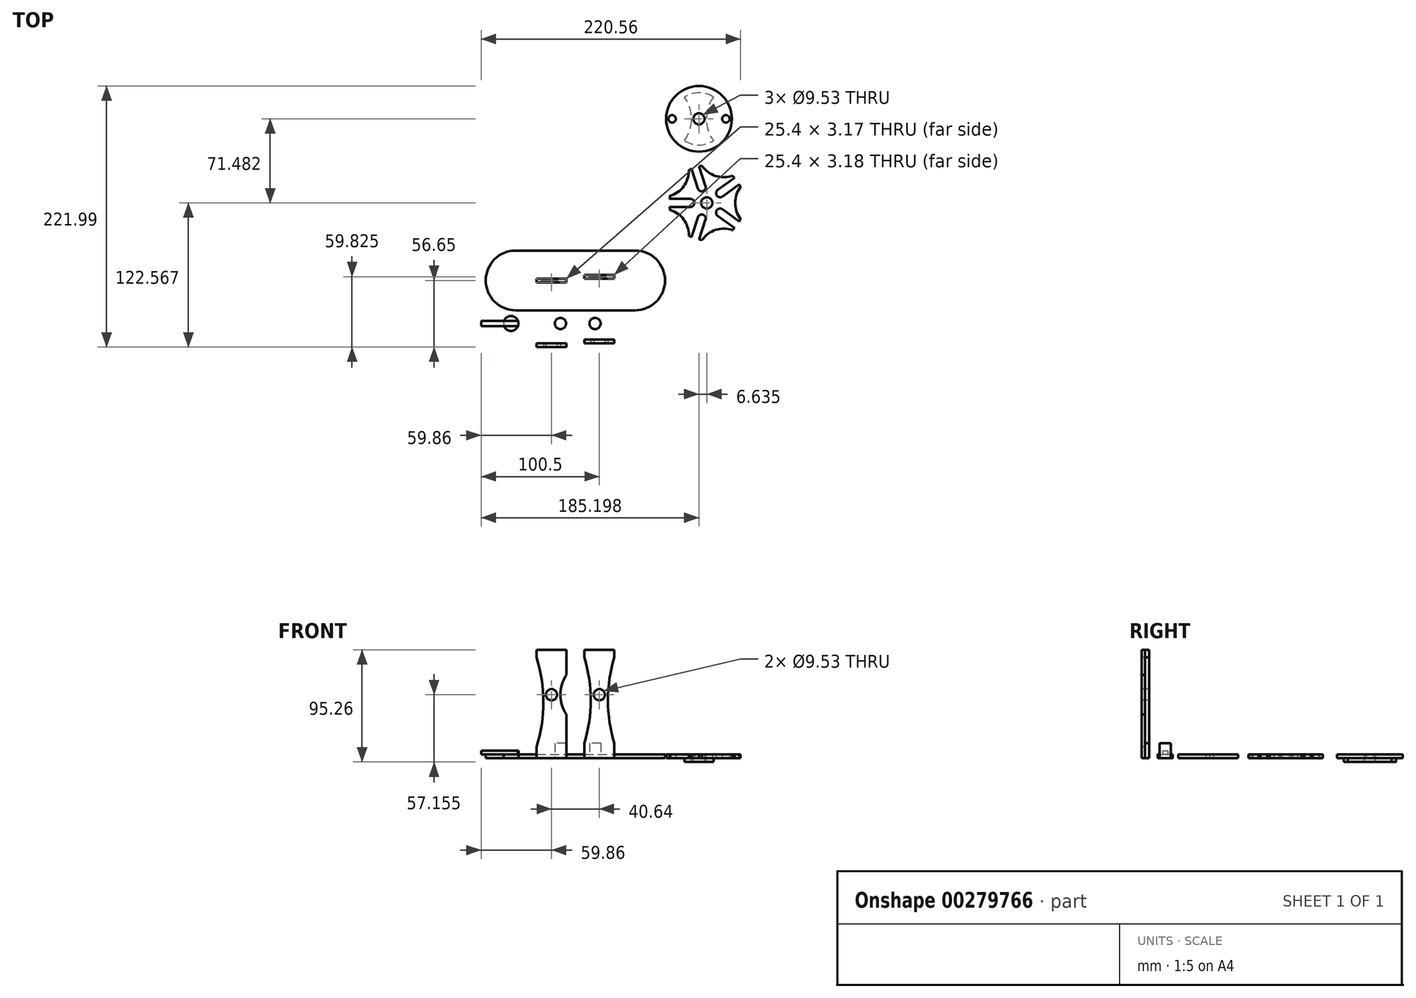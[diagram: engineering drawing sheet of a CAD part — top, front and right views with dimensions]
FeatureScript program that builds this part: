
annotation { "Feature Type Name" : "Feature", "Feature Type Description" : "" }
export const myFeature = defineFeature(function(context is Context, id is Id, definition is map)
    precondition{}
    {
        {
            var Q0;
            Q0=qCreatedBy(makeId("Top.planeOp"),FACE);
            var sketch = newSketch(context, id + "F0", { "sketchPlane" : qUnion([Q0])});
            skArc(sketch, "E0", {"start": v(-38.1, 25.4) * mm, "mid": v(-63.5, 0) * mm, "end": v(-38.1, -25.4) * mm});
            skArc(sketch, "E1", {"start": v(63.5, -25.4) * mm, "mid": v(88.9, 0) * mm, "end": v(63.5, 25.4) * mm});
            skLineSegment(sketch, "E2", {"start": v(-38.1, 25.4) * mm, "end": v(63.5, 25.4) * mm});
            skLineSegment(sketch, "E3", {"start": v(-38.1, -25.4) * mm, "end": v(63.5, -25.4) * mm});
            skSolve(sketch);
        }
        {
            var Q0;
            Q0=makeQuery(id+"F0.imprint","IMPRINT",FACE,{"disambiguationData":[TD([[makeQuery(id+"F0.imprint","IMPRINT",EDGE,{"derivedFrom":sQuery(id+"F0.wireOp",EDGE,"E0")}),1.0]])]});
            extrude(context, id + "F1", {"entities" : qUnion([Q0]), "depth" : 3.17 * mm});
        }
        {
            var Q0;
            Q0=qCreatedBy(makeId("Top.planeOp"),FACE);
            var sketch = newSketch(context, id + "F2", { "sketchPlane" : qUnion([Q0])});
            skCircle(sketch, "E4", {"center": v(117.72, 137.4) * mm, "radius": 27.94 * mm});
            skArc(sketch, "E5", {"start": v(130.02, 155.9) * mm, "mid": v(117.72, 159.62) * mm, "end": v(105.42, 155.9) * mm});
            skArc(sketch, "E6", {"start": v(146.1, 42.78) * mm, "mid": v(147, 43.67) * mm, "end": v(147.87, 44.6) * mm});
            skArc(sketch, "E7", {"start": v(120.36, 97.42) * mm, "mid": v(131.8, 88.87) * mm, "end": v(146.1, 89.05) * mm});
            skArc(sketch, "E8", {"start": v(93.16, 71.85) * mm, "mid": v(104.83, 80.1) * mm, "end": v(109.07, 93.75) * mm});
            skArc(sketch, "E9", {"start": v(109.07, 38.09) * mm, "mid": v(104.83, 51.73) * mm, "end": v(93.16, 59.98) * mm});
            skArc(sketch, "E10", {"start": v(146.1, 42.78) * mm, "mid": v(131.8, 42.97) * mm, "end": v(120.36, 34.42) * mm});
            skArc(sketch, "E11.trimOffspring", {"start": v(109.07, 38.09) * mm, "mid": v(110.2, 37.5) * mm, "end": v(111.34, 36.96) * mm});
            skArc(sketch, "E12.trimOffspring", {"start": v(153.08, 79.45) * mm, "mid": v(152.51, 80.58) * mm, "end": v(151.9, 81.7) * mm});
            skArc(sketch, "E13.trimOffspring", {"start": v(93.16, 71.85) * mm, "mid": v(92.95, 70.6) * mm, "end": v(92.79, 69.35) * mm});
            skArc(sketch, "E14.trimOffspring", {"start": v(120.36, 97.42) * mm, "mid": v(119.1, 97.23) * mm, "end": v(117.86, 97) * mm});
            skPoint(sketch, "E15", {"position": v(170.7, 65.92) * mm});
            skArc(sketch, "E16", {"start": v(153.08, 79.45) * mm, "mid": v(148.48, 65.92) * mm, "end": v(153.08, 52.39) * mm});
            skPoint(sketch, "E17", {"position": v(92.6, 65.92) * mm});
            skPoint(sketch, "E18", {"position": v(114.54, 35.72) * mm});
            skPoint(sketch, "E19", {"position": v(150.04, 47.26) * mm});
            skPoint(sketch, "E20", {"position": v(150.04, 84.58) * mm});
            skPoint(sketch, "E21", {"position": v(114.54, 96.11) * mm});
            skCircle(sketch, "E22", {"center": v(94.86, 137.4) * mm, "radius": 3.18 * mm});
            skPoint(sketch, "E23", {"position": v(110.38, 65.92) * mm});
            skArc(sketch, "E24.trimOffspring", {"start": v(92.79, 62.49) * mm, "mid": v(92.95, 61.23) * mm, "end": v(93.16, 59.98) * mm});
            skArc(sketch, "E25.trimOffspring", {"start": v(111.34, 94.88) * mm, "mid": v(110.2, 94.33) * mm, "end": v(109.07, 93.75) * mm});
            skArc(sketch, "E26.trimOffspring", {"start": v(147.87, 87.24) * mm, "mid": v(147, 88.17) * mm, "end": v(146.1, 89.05) * mm});
            skArc(sketch, "E27.trimOffspring", {"start": v(151.9, 50.14) * mm, "mid": v(152.51, 51.25) * mm, "end": v(153.08, 52.39) * mm});
            skArc(sketch, "E28.trimOffspring", {"start": v(117.86, 34.84) * mm, "mid": v(119.1, 34.6) * mm, "end": v(120.36, 34.42) * mm});
            skCircle(sketch, "E29", {"center": v(124.35, 65.92) * mm, "radius": 4.76 * mm});
            skCircle(sketch, "E30", {"center": v(117.72, 137.4) * mm, "radius": 4.76 * mm});
            skCircle(sketch, "E31", {"center": v(140.58, 137.4) * mm, "radius": 3.18 * mm});
            skArc(sketch, "E32", {"start": v(130.02, 155.9) * mm, "mid": v(124.07, 137.4) * mm, "end": v(130.02, 118.9) * mm});
            skArc(sketch, "E33", {"start": v(105.42, 118.9) * mm, "mid": v(111.37, 137.4) * mm, "end": v(105.42, 155.9) * mm});
            skArc(sketch, "E34.trimOffspring", {"start": v(105.42, 118.9) * mm, "mid": v(117.72, 115.17) * mm, "end": v(130.02, 118.9) * mm});
            skPoint(sketch, "E35.end.orphan", {"position": v(110.38, 62.49) * mm});
            skPoint(sketch, "E35.start.orphan", {"position": v(110.38, 69.35) * mm});
            skPoint(sketch, "E36", {"position": v(93.16, 65.92) * mm});
            skArc(sketch, "E37", {"start": v(110.38, 69.35) * mm, "mid": v(113.81, 65.92) * mm, "end": v(110.38, 62.49) * mm});
            skLineSegment(sketch, "E38", {"start": v(110.38, 69.35) * mm, "end": v(92.79, 69.35) * mm});
            skLineSegment(sketch, "E39", {"start": v(110.38, 62.49) * mm, "end": v(92.79, 62.49) * mm});
            skLineSegment(sketch, "E40.1.0", {"start": v(123.3, 80.26) * mm, "end": v(117.86, 97) * mm});
            skArc(sketch, "E40.1.1", {"start": v(123.3, 80.26) * mm, "mid": v(121.1, 75.94) * mm, "end": v(116.78, 78.14) * mm});
            skLineSegment(sketch, "E40.1.2", {"start": v(116.78, 78.14) * mm, "end": v(111.34, 94.88) * mm});
            skLineSegment(sketch, "E40.2.0", {"start": v(137.67, 71.35) * mm, "end": v(151.9, 81.7) * mm});
            skArc(sketch, "E40.2.1", {"start": v(137.67, 71.35) * mm, "mid": v(132.88, 72.11) * mm, "end": v(133.64, 76.9) * mm});
            skLineSegment(sketch, "E40.2.2", {"start": v(133.64, 76.9) * mm, "end": v(147.87, 87.24) * mm});
            skLineSegment(sketch, "E40.3.0", {"start": v(133.64, 54.93) * mm, "end": v(147.87, 44.6) * mm});
            skArc(sketch, "E40.3.1", {"start": v(133.64, 54.93) * mm, "mid": v(132.88, 59.72) * mm, "end": v(137.67, 60.48) * mm});
            skLineSegment(sketch, "E40.3.2", {"start": v(137.67, 60.48) * mm, "end": v(151.9, 50.14) * mm});
            skLineSegment(sketch, "E40.4.0", {"start": v(116.78, 53.7) * mm, "end": v(111.34, 36.96) * mm});
            skArc(sketch, "E40.4.1", {"start": v(116.78, 53.7) * mm, "mid": v(121.1, 55.9) * mm, "end": v(123.3, 51.57) * mm});
            skLineSegment(sketch, "E40.4.2", {"start": v(123.3, 51.57) * mm, "end": v(117.86, 34.84) * mm});
            skLineSegment(sketch, "E40.anchor1", {"start": v(124.35, 65.92) * mm, "end": v(92.79, 69.35) * mm, "construction": true});
            skLineSegment(sketch, "E40.anchor2", {"start": v(124.35, 65.92) * mm, "end": v(111.34, 36.96) * mm, "construction": true});
            skSolve(sketch);
        }
        {
            var Q0;
            Q0=makeQuery(id+"F1.opExtrude","CAP_FACE",FACE,{"disambiguationData":[OSD([sQuery(id+"F0.wireOp",EDGE,"E0"),sQuery(id+"F0.wireOp",EDGE,"E1"),sQuery(id+"F0.wireOp",EDGE,"E2"),sQuery(id+"F0.wireOp",EDGE,"E3")])],"isStart":false});
            var sketch = newSketch(context, id + "F3", { "sketchPlane" : qUnion([Q0])});
            skSolve(sketch);
        }
        {
            var Q0;
            Q0=makeQuery(id+"F2.imprint","IMPRINT",FACE,{"disambiguationData":[TD([[makeQuery(id+"F2.imprint","IMPRINT",EDGE,{"derivedFrom":sQuery(id+"F2.wireOp",EDGE,"E6")}),1.0]])]});
            extrude(context, id + "F4", {"entities" : qUnion([Q0]), "depth" : 3.17 * mm});
        }
        {
            var Q0;
            Q0=makeQuery(id+"F2.imprint","IMPRINT",FACE,{"disambiguationData":[TD([[makeQuery(id+"F2.imprint","IMPRINT",EDGE,{"derivedFrom":sQuery(id+"F2.wireOp",EDGE,"E5")}),1.0]])]});
            extrude(context, id + "F5", {"entities" : qUnion([Q0]), "depth" : 3.17 * mm});
        }
        {
            var Q0;
            Q0=makeQuery(id+"F2.imprint","IMPRINT",FACE,{"disambiguationData":[TD([[makeQuery(id+"F2.imprint","IMPRINT",EDGE,{"derivedFrom":sQuery(id+"F2.wireOp",EDGE,"E4")}),1.0]])]});
            extrude(context, id + "F6", {"entities" : qUnion([Q0]), "operationType" : NewBodyOperationType.ADD, "depth" : 3.17 * mm});
        }
        {
            var Q0;
            Q0=makeQuery(id+"F3.imprint","IMPRINT",FACE,{"disambiguationData":[TD([[makeQuery(id+"F3.imprint","IMPRINT",EDGE,{"derivedFrom":makeQuery(id+"F1.opExtrude","CAP_EDGE",EDGE,{"disambiguationData":[OSD([sQuery(id+"F0.wireOp",EDGE,"E0")])],"isStart":false})}),1.0]])]});
            var sketch = newSketch(context, id + "F7", { "sketchPlane" : qUnion([Q0])});
            skPoint(sketch, "E41", {"position": v(-38.1, 25.4) * mm});
            skPoint(sketch, "E42", {"position": v(63.5, 25.4) * mm});
            skLineSegment(sketch, "E43", {"start": v(-38.1, 25.4) * mm, "end": v(63.5, 25.4) * mm});
            skPoint(sketch, "E44", {"position": v(12.7, 25.4) * mm});
            skPoint(sketch, "E45", {"position": v(12.7, 0) * mm});
            skPoint(sketch, "E46", {"position": v(-7.62, 0) * mm});
            skLineSegment(sketch, "E47.bottom", {"start": v(-20.32, -1.59) * mm, "end": v(5.08, -1.59) * mm});
            skLineSegment(sketch, "E47.left", {"start": v(-20.32, -1.59) * mm, "end": v(-20.32, 1.59) * mm});
            skLineSegment(sketch, "E47.right", {"start": v(5.08, -1.59) * mm, "end": v(5.08, 1.59) * mm});
            skLineSegment(sketch, "E48.top", {"start": v(20.32, 1.59) * mm, "end": v(45.72, 1.59) * mm});
            skLineSegment(sketch, "E49", {"start": v(20.32, 1.59) * mm, "end": v(20.32, 4.76) * mm});
            skLineSegment(sketch, "E50", {"start": v(20.32, 4.76) * mm, "end": v(45.72, 4.76) * mm});
            skLineSegment(sketch, "E51", {"start": v(45.72, 4.76) * mm, "end": v(45.72, 1.59) * mm});
            skPoint(sketch, "E52", {"position": v(33.02, 0) * mm});
            skLineSegment(sketch, "E53", {"start": v(-20.32, 1.59) * mm, "end": v(5.08, 1.59) * mm});
            skLineSegment(sketch, "E54", {"start": v(5.08, -53.47) * mm, "end": v(5.08, -56.65) * mm});
            skLineSegment(sketch, "E55", {"start": v(5.08, -56.65) * mm, "end": v(-20.32, -56.65) * mm});
            skLineSegment(sketch, "E56", {"start": v(-20.32, -56.65) * mm, "end": v(-20.32, -53.47) * mm});
            skLineSegment(sketch, "E57", {"start": v(-20.32, -53.47) * mm, "end": v(5.08, -53.47) * mm});
            skLineSegment(sketch, "E58", {"start": v(20.32, -53.47) * mm, "end": v(20.32, -50.3) * mm});
            skLineSegment(sketch, "E59", {"start": v(20.32, -50.3) * mm, "end": v(45.72, -50.3) * mm});
            skLineSegment(sketch, "E60", {"start": v(45.72, -50.3) * mm, "end": v(45.72, -53.47) * mm});
            skLineSegment(sketch, "E61", {"start": v(45.72, -53.47) * mm, "end": v(20.32, -53.47) * mm});
            skPoint(sketch, "E62", {"position": v(33.02, 4.76) * mm});
            skSolve(sketch);
        }
        {
            var Q0;
            Q0=makeQuery(id+"F2.imprint","IMPRINT",FACE,{"disambiguationData":[TD([[makeQuery(id+"F2.imprint","IMPRINT",EDGE,{"derivedFrom":sQuery(id+"F2.wireOp",EDGE,"E6")}),1.0]])]});
            extrude(context, id + "F8", {"entities" : qUnion([Q0]), "operationType" : NewBodyOperationType.ADD, "depth" : 3.17 * mm});
        }
        {
            var Q0;
            Q0=makeQuery(id+"F7.imprint","IMPRINT",FACE,{"disambiguationData":[TD([[makeQuery(id+"F7.imprint","IMPRINT",EDGE,{"derivedFrom":sQuery(id+"F7.wireOp",EDGE,"E47.bottom")}),1.0]])]});
            extrude(context, id + "F9", {"entities" : qUnion([Q0]), "operationType" : NewBodyOperationType.REMOVE, "oppositeDirection" : true, "depth" : 3.17 * mm});
        }
        {
            var Q0;
            Q0=makeQuery(id+"F7.imprint","IMPRINT",FACE,{"disambiguationData":[TD([[makeQuery(id+"F7.imprint","IMPRINT",EDGE,{"derivedFrom":sQuery(id+"F7.wireOp",EDGE,"E48.top")}),1.0]])]});
            extrude(context, id + "F10", {"entities" : qUnion([Q0]), "operationType" : NewBodyOperationType.REMOVE, "oppositeDirection" : true, "depth" : 3.17 * mm});
        }
        {
            var Q0;
            Q0=makeQuery(id+"F7.imprint","IMPRINT",FACE,{"disambiguationData":[TD([[makeQuery(id+"F7.imprint","IMPRINT",EDGE,{"derivedFrom":sQuery(id+"F7.wireOp",EDGE,"E54")}),-1.0]])]});
            var Q1;
            Q1=makeQuery(id+"F7.imprint","IMPRINT",FACE,{"disambiguationData":[TD([[makeQuery(id+"F7.imprint","IMPRINT",EDGE,{"derivedFrom":sQuery(id+"F7.wireOp",EDGE,"E58")}),-1.0]])]});
            extrude(context, id + "F11", {"entities" : qUnion([Q0, Q1]), "depth" : 88.9 * mm});
        }
        {
            var Q0;
            Q0=makeQuery(id+"F11.opExtrude","SWEPT_FACE",FACE,{"disambiguationData":[OSD([sQuery(id+"F7.wireOp",EDGE,"E61")])]});
            var sketch = newSketch(context, id + "F12", { "sketchPlane" : qUnion([Q0])});
            skLineSegment(sketch, "E63", {"start": v(20.32, 6.35) * mm, "end": v(20.32, 12.7) * mm});
            skLineSegment(sketch, "E64", {"start": v(45.72, 12.7) * mm, "end": v(45.72, 6.35) * mm});
            skLineSegment(sketch, "E65", {"start": v(20.32, 92.08) * mm, "end": v(20.32, 85.73) * mm});
            skLineSegment(sketch, "E66", {"start": v(45.72, 92.08) * mm, "end": v(45.72, 85.73) * mm});
            skArc(sketch, "E67", {"start": v(20.32, 12.7) * mm, "mid": v(25.68, 49.21) * mm, "end": v(20.32, 85.73) * mm});
            skArc(sketch, "E68", {"start": v(45.72, 85.73) * mm, "mid": v(40.36, 49.21) * mm, "end": v(45.72, 12.7) * mm});
            skPoint(sketch, "E69", {"position": v(33.02, 92.08) * mm});
            skPoint(sketch, "E70", {"position": v(33.02, 53.98) * mm});
            skCircle(sketch, "E71", {"center": v(33.02, 53.98) * mm, "radius": 4.76 * mm});
            skSolve(sketch);
        }
        {
            var Q0;
            Q0=makeQuery(id+"F7.imprint","IMPRINT",FACE,{"disambiguationData":[TD([[makeQuery(id+"F7.imprint","IMPRINT",EDGE,{"derivedFrom":sQuery(id+"F7.wireOp",EDGE,"E54")}),-1.0]])]});
            extrude(context, id + "F13", {"entities" : qUnion([Q0]), "operationType" : NewBodyOperationType.ADD, "oppositeDirection" : true, "depth" : 3.17 * mm});
        }
        {
            var Q0;
            Q0=makeQuery(id+"F7.imprint","IMPRINT",FACE,{"disambiguationData":[TD([[makeQuery(id+"F7.imprint","IMPRINT",EDGE,{"derivedFrom":sQuery(id+"F7.wireOp",EDGE,"E58")}),-1.0]])]});
            extrude(context, id + "F14", {"entities" : qUnion([Q0]), "operationType" : NewBodyOperationType.ADD, "oppositeDirection" : true, "depth" : 3.17 * mm});
        }
        {
            var Q0;
            {var subQ0=sQuery(id+"F7.wireOp",EDGE,"E55");Q0=makeQuery(id+"F13.boolean.opBoolean","MERGE",FACE,{"derivedFrom":[makeQuery(id+"F11.opExtrude","SWEPT_FACE",FACE,{"disambiguationData":[OSD([subQ0])]}),makeQuery(id+"F13.opExtrude","SWEPT_FACE",FACE,{"disambiguationData":[OSD([subQ0])]})]});}
            var sketch = newSketch(context, id + "F15", { "sketchPlane" : qUnion([Q0])});
            skPoint(sketch, "E72", {"position": v(-7.62, 92.08) * mm});
            skPoint(sketch, "E73", {"position": v(-7.62, 53.98) * mm});
            skPoint(sketch, "E74", {"position": v(30.48, 53.98) * mm});
            skArc(sketch, "E75", {"start": v(5.08, 70.82) * mm, "mid": v(0, 53.98) * mm, "end": v(5.08, 37.13) * mm});
            skLineSegment(sketch, "E76", {"start": v(-20.32, 3.18) * mm, "end": v(-20.32, 9.53) * mm});
            skLineSegment(sketch, "E77", {"start": v(-20.32, 92.08) * mm, "end": v(-20.32, 85.73) * mm});
            skArc(sketch, "E78", {"start": v(-20.32, 9.53) * mm, "mid": v(-14.47, 47.63) * mm, "end": v(-20.32, 85.72) * mm});
            skCircle(sketch, "E79", {"center": v(-7.62, 53.98) * mm, "radius": 4.76 * mm});
            skSolve(sketch);
        }
        {
            var Q0;
            {var subQ0=sQuery(id+"F15.wireOp",EDGE,"E75");Q0=makeQuery(id+"F15.imprint","IMPRINT",FACE,{"disambiguationData":[TD([[makeQuery(id+"F15.imprint","IMPRINT",EDGE,{"derivedFrom":subQ0}),1.0]])]});}
            var Q1;
            {var subQ0=sQuery(id+"F15.wireOp",EDGE,"E78");Q1=makeQuery(id+"F15.imprint","IMPRINT",FACE,{"disambiguationData":[TD([[makeQuery(id+"F15.imprint","IMPRINT",EDGE,{"derivedFrom":subQ0}),1.0]])]});}
            extrude(context, id + "F16", {"entities" : qUnion([Q0, Q1]), "operationType" : NewBodyOperationType.REMOVE, "oppositeDirection" : true, "depth" : 3.17 * mm});
        }
        {
            var Q0;
            {var subQ0=sQuery(id+"F12.wireOp",EDGE,"E67");Q0=makeQuery(id+"F12.imprint","IMPRINT",FACE,{"disambiguationData":[TD([[makeQuery(id+"F12.imprint","IMPRINT",EDGE,{"derivedFrom":subQ0}),1.0]])]});}
            var Q1;
            {var subQ0=sQuery(id+"F12.wireOp",EDGE,"E68");Q1=makeQuery(id+"F12.imprint","IMPRINT",FACE,{"disambiguationData":[TD([[makeQuery(id+"F12.imprint","IMPRINT",EDGE,{"derivedFrom":subQ0}),1.0]])]});}
            extrude(context, id + "F17", {"entities" : qUnion([Q0, Q1]), "operationType" : NewBodyOperationType.REMOVE, "oppositeDirection" : true, "depth" : 3.17 * mm});
        }
        {
            var Q0;
            Q0=makeQuery(id+"F12.imprint","IMPRINT",FACE,{"disambiguationData":[TD([[makeQuery(id+"F12.imprint","IMPRINT",EDGE,{"derivedFrom":sQuery(id+"F12.wireOp",EDGE,"E71")}),1.0]])]});
            extrude(context, id + "F18", {"entities" : qUnion([Q0]), "operationType" : NewBodyOperationType.REMOVE, "oppositeDirection" : true, "depth" : 3.17 * mm});
        }
        {
            var Q0;
            Q0=makeQuery(id+"F15.imprint","IMPRINT",FACE,{"disambiguationData":[TD([[makeQuery(id+"F15.imprint","IMPRINT",EDGE,{"derivedFrom":sQuery(id+"F15.wireOp",EDGE,"E79")}),1.0]])]});
            extrude(context, id + "F19", {"entities" : qUnion([Q0]), "operationType" : NewBodyOperationType.REMOVE, "oppositeDirection" : true, "depth" : 3.17 * mm});
        }
        {
            var Q0;
            Q0=makeQuery(id+"F2.imprint","IMPRINT",FACE,{"disambiguationData":[TD([[makeQuery(id+"F2.imprint","IMPRINT",EDGE,{"derivedFrom":sQuery(id+"F2.wireOp",EDGE,"E5")}),1.0]])]});
            extrude(context, id + "F20", {"entities" : qUnion([Q0]), "oppositeDirection" : true, "depth" : 3.17 * mm});
        }
        {
            var Q0;
            Q0=qCreatedBy(makeId("Top.planeOp"),FACE);
            var sketch = newSketch(context, id + "F21", { "sketchPlane" : qUnion([Q0])});
            skPoint(sketch, "E80", {"position": v(0, -36.61) * mm});
            skPoint(sketch, "E81", {"position": v(29.4, -36.61) * mm});
            skCircle(sketch, "E82", {"center": v(0, -36.61) * mm, "radius": 4.76 * mm});
            skCircle(sketch, "E83", {"center": v(29.4, -36.61) * mm, "radius": 4.76 * mm});
            skPoint(sketch, "E84", {"position": v(-42.08, -36.61) * mm});
            skCircle(sketch, "E85", {"center": v(-42.08, -36.61) * mm, "radius": 6.35 * mm});
            skSolve(sketch);
        }
        {
            var Q0;
            Q0=makeQuery(id+"F21.imprint","IMPRINT",FACE,{"disambiguationData":[TD([[makeQuery(id+"F21.imprint","IMPRINT",EDGE,{"derivedFrom":sQuery(id+"F21.wireOp",EDGE,"E83")}),1.0]])]});
            extrude(context, id + "F22", {"entities" : qUnion([Q0]), "depth" : 12.7 * mm});
        }
        {
            var Q0;
            Q0=makeQuery(id+"F21.imprint","IMPRINT",FACE,{"disambiguationData":[TD([[makeQuery(id+"F21.imprint","IMPRINT",EDGE,{"derivedFrom":sQuery(id+"F21.wireOp",EDGE,"E85")}),1.0]])]});
            extrude(context, id + "F23", {"entities" : qUnion([Q0]), "depth" : 3.17 * mm});
        }
        {
            var Q0;
            Q0=makeQuery(id+"F23.opExtrude","CAP_FACE",FACE,{"disambiguationData":[OSD([sQuery(id+"F21.wireOp",EDGE,"E85")])],"isStart":false});
            var sketch = newSketch(context, id + "F24", { "sketchPlane" : qUnion([Q0])});
            skLineSegment(sketch, "E86.bottom", {"start": v(-67.48, -38.84) * mm, "end": v(-16.68, -38.84) * mm});
            skLineSegment(sketch, "E86.top", {"start": v(-67.48, -34.4) * mm, "end": v(-16.68, -34.4) * mm});
            skLineSegment(sketch, "E86.left", {"start": v(-67.48, -38.84) * mm, "end": v(-67.48, -34.4) * mm});
            skLineSegment(sketch, "E86.right", {"start": v(-16.68, -38.84) * mm, "end": v(-16.68, -34.4) * mm});
            skPoint(sketch, "E86.middle", {"position": v(-42.08, -36.61) * mm});
            skSolve(sketch);
        }
        {
            var Q0;
            {var subQ0=sQuery(id+"F24.wireOp",EDGE,"E86.left");Q0=makeQuery(id+"F24.imprint","IMPRINT",FACE,{"disambiguationData":[TD([[makeQuery(id+"F24.imprint","IMPRINT",EDGE,{"derivedFrom":subQ0}),-1.0]])]});}
            var Q1;
            {var subQ0=sQuery(id+"F24.wireOp",EDGE,"E86.bottom");var subQ1=makeQuery(id+"F23.opExtrude","CAP_EDGE",EDGE,{"disambiguationData":[OSD([sQuery(id+"F21.wireOp",EDGE,"E85")])],"isStart":false});var subQ2=makeQuery(id+"F24.imprint","INTERSECT",VERTEX,{"disambiguationData":[OD(0.0)],"derivedFrom":[subQ1,subQ0]});Q1=makeQuery(id+"F24.imprint","IMPRINT",FACE,{"disambiguationData":[TD([[makeQuery(id+"F24.imprint","IMPRINT",EDGE,{"disambiguationData":[TD([[subQ2,-1.0]])],"derivedFrom":subQ0}),1.0]])]});}
            extrude(context, id + "F25", {"entities" : qUnion([Q0, Q1]), "depth" : 3.17 * mm});
        }
        {
            var Q0;
            Q0=makeQuery(id+"F21.imprint","IMPRINT",FACE,{"disambiguationData":[TD([[makeQuery(id+"F21.imprint","IMPRINT",EDGE,{"derivedFrom":sQuery(id+"F21.wireOp",EDGE,"E82")}),1.0]])]});
            extrude(context, id + "F26", {"entities" : qUnion([Q0]), "depth" : 12.7 * mm});
        }
    });
